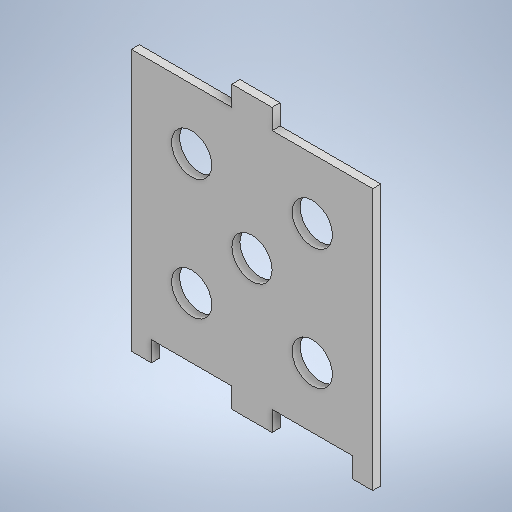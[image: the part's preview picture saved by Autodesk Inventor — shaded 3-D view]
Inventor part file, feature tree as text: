
AUTODESK INVENTOR PART (.ipt)
format: ipt  version: 2025.1 (Build 291241020, 241B)  size: 286,720 bytes
history: native  units: in
note: dims shown in document units (in); Inventor stores cm internally (conversion verified against a paired STEP export)
features: extrude x2, sketch x2
ambient origin geometry x8: Origin, YZ Plane, XZ Plane, XY Plane, X Axis, Y Axis, Z Axis, Center Point
bodies: Solid1 (feature_tree)
feature tree (4):
  extrude  "Extrusion1"  Depth=6.0in
  extrude  "Extrusion2"  Depth=0.5in
  sketch  "Sketch1"  dims[d0=6.0in d1=6.0in]
  sketch  "Sketch2"  dims[d5=0.5in d6=0.5in d7=0.5in d8=0.5in d9=2.5in d10=90.0deg d11=1.0in d12=1.0in d13=1.0in d14=1.0in d15=1.0in d16=1.5in d17=1.5in d18=1.5in d19=1.5in d20=3.0in d21=3.0in d22=1.5in d23=1.5in d24=1.5in d25=1.5in d26=0.5in d27=0.2in d28=0.0in d29=0.5in d31=0.5in d32=0.5in d33=0.0in]
